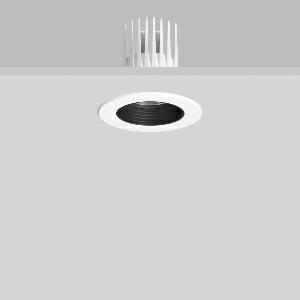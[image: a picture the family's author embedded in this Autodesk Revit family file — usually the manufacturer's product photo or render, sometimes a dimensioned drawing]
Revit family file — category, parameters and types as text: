
# Revit family: heledon_mini_e_901745_002_2_e577
name_source: partatom
category: Lighting Fixtures
units: mm (PartAtom-declared; Revit-internal decimal feet)

## family parameters
Cut with Voids When Loaded = No
Host = Face
Light Source = No
Part Type = Normal
Room Calculation Point = No
Round Connector Dimension = Use Diameter
Shared = No

## types (1)
- HELEDON mini E (1 x LED Modul 927, 1900 lm, 2700)
    Apparent Load = 20 VA
    Approval mark = CE
    CIE Flux Codes = 98 100 100 100 100
    Color Rendering = 92
    Color Temperature = 2700
    Default Elevation = 1800 mm
    Description = Series: HELEDON mini
Round recessed downlight. Housing: die-cast aluminium, powder-coated. Black plastic ring and recessed LED to prevent glare from the side. Optical assembly with lens made of plastic (polycarbonate) for the best homogeneous light distribution - can be changed without tools. Best colour rendering index Ra>90. Suitable for Recessed ceiling mounting. Installation without tools thanks to spring fastening system. Including separate LED converter with connecting cable 600 mm.High quality converter without flickering and stroboscopic effect. Through-wiring box (5 pole) available as accessory. The following accessories can be mounted without use of tools: interchangeable lenses, decorative glasses, honeycomb louvre, clear and frosted diffusers, white interchangeable plastic ring. 
Colour: traffic white, matt (RAL 9016)
Diameter: 124 mm
Height: 3 mm
Cut-out diameter: 114 mm
Recess height: 170 mm
Luminaire: recess height: 120 mm
Lamp: LED
Socket: without socket
Colour temperature: 2700K
Colour rendering index (CRI): 92
System power: 20 W
Rated luminous flux: 1900 lm
Luminous efficiency: 95 lm/W
Control gear: Regulated power supply
Protection class: II
Type of protection: IP 20
    Height = 0 mm  [stored 0 ft]
    Lamp = 1 x LED Modul 927
    Lamp Light Flux = 1900 lm
    Lamp count = 1
    Length = 124 mm  [stored 0.406824 ft]
    Lifetime = 50000 h
    Luminous efficacy = 95 lm/W
    Manufacturer = RZB
    ModVariant = No
    Model = 901745.002.2
    Mounting Place = Ceiling
    Mounting Type = Recessed
    Number of Poles = 1
    OnlyDefault = Yes
    Power Factor = 1
    Product Name = HELEDON mini E
    Product group = Recessed downlights
    ProductGroupID = 402
    Protection Class = Protection class II
    Protection Degree = IP 20
    RLX_Detail_Level = 1
    RLX_Emergency_Light_Flux = 0 lm
    RLX_Emergency_Type = 0
    RLX_Emergency_Type_DB = No
    RlxData = <blob elided: 127261 chars, md5=b730fdb8>
    Socket = socket
    Standby Power = 0 W
    System Light Flux = 1900 lm
    System Power = 20 W
    Type Comments = Product without accessories
    Type Image = 901656.002.jpg
    URL = http://relux.com
    VarID = ---
    Voltage = 230 V
    Voltage Range = 220-240 V
    Weight = 0.00 kg
    Width = 0 mm  [stored 0 ft]

note: [stored X ft] marks values corroborated as IEEE doubles in the binary element streams (Revit-internal decimal feet)

## geometry (parser evidence)
native form markers: Blend x4, Sweep x12
no freeform markers — native parametric forms only
